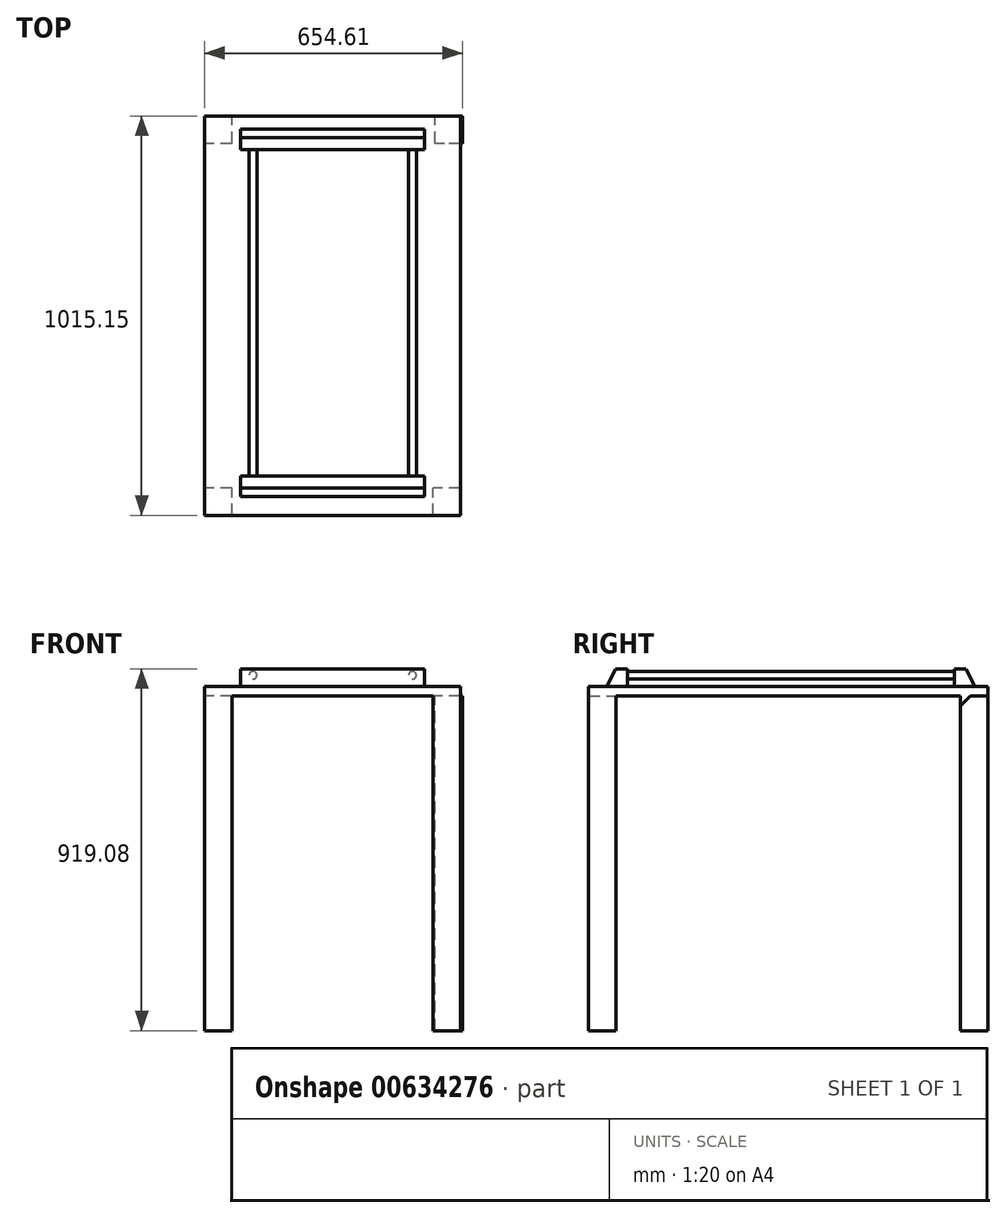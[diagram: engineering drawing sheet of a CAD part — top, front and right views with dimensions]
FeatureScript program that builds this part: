
annotation { "Feature Type Name" : "Feature", "Feature Type Description" : "" }
export const myFeature = defineFeature(function(context is Context, id is Id, definition is map)
    precondition{}
    {
        {
            var Q0;
            Q0=qCreatedBy(makeId("Front.planeOp"),FACE);
            var sketch = newSketch(context, id + "F0", { "sketchPlane" : qUnion([Q0])});
            skCircle(sketch, "E0", {"center": v(-202.55, -35.12) * mm, "radius": 9.95 * mm});
            skSolve(sketch);
        }
        {
            var Q0;
            Q0=qCreatedBy(makeId("Right.planeOp"),FACE);
            var Q1;
            Q1=sQuery(id+"F0.wireOp",VERTEX,"E0.center");
            cPlane(context, id + "F1", {"entities" : qUnion([Q0, Q1]), "cplaneType" : CPlaneType.PLANE_POINT, "offset" : 25 * mm, "width" : 150 * mm, "height" : 150 * mm});
        }
        {
            var Q0;
            Q0=qCreatedBy(makeId("Front.planeOp"),FACE);
            cPlane(context, id + "F2", {"entities" : qUnion([Q0]), "cplaneType" : CPlaneType.OFFSET, "offset" : 242.37 * mm, "width" : 150 * mm, "height" : 150 * mm});
        }
        {
            var Q0;
            Q0=qCreatedBy(id+"F1.planeOp",FACE);
            var sketch = newSketch(context, id + "F3", { "sketchPlane" : qUnion([Q0])});
            skLineSegment(sketch, "E1", {"start": v(0, -35.42) * mm, "end": v(172.63, -35.42) * mm});
            skLineSegment(sketch, "E2", {"start": v(0, -35.42) * mm, "end": v(-657.37, -35.42) * mm});
            skSolve(sketch);
        }
        {
            var Q0;
            Q0=makeQuery(id+"F0.imprint","IMPRINT",FACE,{"disambiguationData":[TD([[makeQuery(id+"F0.imprint","IMPRINT",EDGE,{"derivedFrom":sQuery(id+"F0.wireOp",EDGE,"E0")}),1.0]])]});
            var Q1;
            Q1=sQuery(id+"F3.wireOp",EDGE,"E2");
            var Q2;
            Q2=sQuery(id+"F3.wireOp",EDGE,"E1");
            sweep(context, id + "F4", {"profiles" : qUnion([Q0]), "path" : qUnion([Q1, Q2])});
        }
        {
            var Q0;
            Q0=makeQuery(id+"F4.opSweep","SWEPT_BODY",BODY,{"disambiguationData":[OSD([sQuery(id+"F0.wireOp",EDGE,"E0"),sQuery(id+"F3.wireOp",EDGE,"E1")])]});
            var Q1;
            Q1=qCreatedBy(makeId("Right.planeOp"),FACE);
            mirror(context, id + "F5", {"operationType" : NewBodyOperationType.ADD, "entities" : qUnion([Q0]), "mirrorPlane" : qUnion([Q1])});
        }
        {
            var Q0;
            Q0=makeQuery(id+"F5.opPattern","COPY",FACE,{"derivedFrom":makeQuery(id+"F4.opSweep","CAP_FACE",FACE,{"disambiguationData":[OSD([sQuery(id+"F0.wireOp",EDGE,"E0"),sQuery(id+"F3.wireOp",VERTEX,"E1.end")])],"isStart":true}),"instanceName":"1"});
            var sketch = newSketch(context, id + "F6", { "sketchPlane" : qUnion([Q0])});
            skLineSegment(sketch, "E3.bottom", {"start": v(-233.82, -19.03) * mm, "end": v(0, -19.03) * mm});
            skLineSegment(sketch, "E3.top", {"start": v(-233.82, -63.11) * mm, "end": v(0, -63.11) * mm});
            skLineSegment(sketch, "E3.left", {"start": v(-233.82, -19.03) * mm, "end": v(-233.82, -63.11) * mm});
            skLineSegment(sketch, "E4.MirrorCS", {"start": v(233.82, -19.03) * mm, "end": v(233.82, -63.11) * mm});
            skLineSegment(sketch, "E5.MirrorCS", {"start": v(233.82, -19.03) * mm, "end": v(0, -19.03) * mm});
            skLineSegment(sketch, "E6.MirrorCS", {"start": v(233.82, -63.11) * mm, "end": v(0, -63.11) * mm});
            skSolve(sketch);
        }
        {
            var Q0;
            Q0 = qSketchRegion(id + "F6", true);
            extrude(context, id + "F7", {"entities" : qUnion([Q0]), "depth" : 55 * mm, "offsetDistance" : 25 * mm});
        }
        {
            var Q0;
            Q0=makeQuery(id+"F7.opExtrude","CAP_EDGE",EDGE,{"disambiguationData":[OSD([sQuery(id+"F6.wireOp",EDGE,"E3.bottom"),sQuery(id+"F6.wireOp",EDGE,"E5.MirrorCS")])],"isStart":false});
            chamfer(context, id + "F8", {"entities" : qUnion([Q0]), "chamferType" : ChamferType.TWO_OFFSETS, "width1" : 25 * mm, "oppositeDirection" : false, "width2" : 50 * mm, "tangentPropagation" : true});
        }
        {
            var Q0;
            Q0=makeQuery(id+"F7.opExtrude","SWEPT_BODY",BODY,{"disambiguationData":[OSD([sQuery(id+"F6.wireOp",EDGE,"E3.bottom"),sQuery(id+"F6.wireOp",EDGE,"E3.top"),sQuery(id+"F6.wireOp",EDGE,"E3.left"),sQuery(id+"F6.wireOp",EDGE,"E4.MirrorCS"),sQuery(id+"F6.wireOp",EDGE,"E5.MirrorCS"),sQuery(id+"F6.wireOp",EDGE,"E6.MirrorCS")])]});
            var Q1;
            Q1=qCreatedBy(id+"F2.planeOp",FACE);
            mirror(context, id + "F9", {"entities" : qUnion([Q0]), "mirrorPlane" : qUnion([Q1])});
        }
        {
            var Q0;
            Q0=makeQuery(id+"F9.opPattern","COPY",FACE,{"derivedFrom":makeQuery(id+"F7.opExtrude","SWEPT_FACE",FACE,{"disambiguationData":[OSD([sQuery(id+"F6.wireOp",EDGE,"E3.top"),sQuery(id+"F6.wireOp",EDGE,"E6.MirrorCS")])]}),"instanceName":"1"});
            var sketch = newSketch(context, id + "F10", { "sketchPlane" : qUnion([Q0])});
            skLineSegment(sketch, "E7.bottom", {"start": v(325.02, 756.89) * mm, "end": v(-325.02, 756.89) * mm});
            skLineSegment(sketch, "E7.top", {"start": v(325.02, -258.26) * mm, "end": v(-325.02, -258.26) * mm});
            skLineSegment(sketch, "E7.left", {"start": v(325.02, 756.89) * mm, "end": v(325.02, -258.26) * mm});
            skLineSegment(sketch, "E7.right", {"start": v(-325.02, 756.89) * mm, "end": v(-325.02, -258.26) * mm});
            skPoint(sketch, "E7.middle", {"position": v(0, 249.31) * mm});
            skPoint(sketch, "E7.middle.positionSnap0", {"position": v(0, 657.37) * mm});
            skPoint(sketch, "E7.centerSnap0", {"position": v(0, 657.37) * mm});
            skSolve(sketch);
        }
        {
            var Q0;
            Q0 = qSketchRegion(id + "F10", true);
            extrude(context, id + "F11", {"entities" : qUnion([Q0]), "depth" : 25 * mm, "offsetDistance" : 25 * mm});
        }
        {
            var Q0;
            Q0=makeQuery(id+"F11.opExtrude","CAP_FACE",FACE,{"disambiguationData":[OSD([sQuery(id+"F10.wireOp",EDGE,"E7.bottom"),sQuery(id+"F10.wireOp",EDGE,"E7.top"),sQuery(id+"F10.wireOp",EDGE,"E7.left"),sQuery(id+"F10.wireOp",EDGE,"E7.right")])],"isStart":false});
            var sketch = newSketch(context, id + "F12", { "sketchPlane" : qUnion([Q0])});
            skLineSegment(sketch, "E8.bottom", {"start": v(325.02, 756.89) * mm, "end": v(255.02, 756.89) * mm});
            skLineSegment(sketch, "E8.top", {"start": v(325.02, 686.89) * mm, "end": v(255.02, 686.89) * mm});
            skLineSegment(sketch, "E8.left", {"start": v(325.02, 756.89) * mm, "end": v(325.02, 686.89) * mm});
            skLineSegment(sketch, "E8.right", {"start": v(255.02, 756.89) * mm, "end": v(255.02, 686.89) * mm});
            skLineSegment(sketch, "E9.bottom", {"start": v(329.59, -188.26) * mm, "end": v(259.59, -188.26) * mm});
            skLineSegment(sketch, "E9.top", {"start": v(329.59, -258.26) * mm, "end": v(259.59, -258.26) * mm});
            skLineSegment(sketch, "E9.left", {"start": v(329.59, -188.26) * mm, "end": v(329.59, -258.26) * mm});
            skLineSegment(sketch, "E9.right", {"start": v(259.59, -188.26) * mm, "end": v(259.59, -258.26) * mm});
            skLineSegment(sketch, "E10.bottom", {"start": v(-255.02, -188.26) * mm, "end": v(-325.02, -188.26) * mm});
            skLineSegment(sketch, "E10.top", {"start": v(-255.02, -258.26) * mm, "end": v(-325.02, -258.26) * mm});
            skLineSegment(sketch, "E10.left", {"start": v(-255.02, -188.26) * mm, "end": v(-255.02, -258.26) * mm});
            skLineSegment(sketch, "E10.right", {"start": v(-325.02, -188.26) * mm, "end": v(-325.02, -258.26) * mm});
            skLineSegment(sketch, "E11.bottom", {"start": v(-255.02, 756.89) * mm, "end": v(-325.02, 756.89) * mm});
            skLineSegment(sketch, "E11.top", {"start": v(-255.02, 686.89) * mm, "end": v(-325.02, 686.89) * mm});
            skLineSegment(sketch, "E11.left", {"start": v(-255.02, 756.89) * mm, "end": v(-255.02, 686.89) * mm});
            skLineSegment(sketch, "E11.right", {"start": v(-325.02, 756.89) * mm, "end": v(-325.02, 686.89) * mm});
            skSolve(sketch);
        }
        {
            var Q0;
            Q0 = qSketchRegion(id + "F12", true);
            extrude(context, id + "F13", {"entities" : qUnion([Q0]), "operationType" : NewBodyOperationType.ADD, "depth" : 850 * mm, "offsetDistance" : 25 * mm});
        }
        {
            var Q0;
            Q0=makeQuery(id+"F13.opExtrude","CAP_EDGE",EDGE,{"disambiguationData":[OSD([sQuery(id+"F12.wireOp",EDGE,"E10.left")])],"isStart":true});
            var Q1;
            Q1=makeQuery(id+"F13.opExtrude","CAP_EDGE",EDGE,{"disambiguationData":[OSD([sQuery(id+"F12.wireOp",EDGE,"E10.bottom")])],"isStart":true});
            var Q2;
            Q2=makeQuery(id+"F13.opExtrude","CAP_EDGE",EDGE,{"disambiguationData":[OSD([sQuery(id+"F12.wireOp",EDGE,"E11.left")])],"isStart":true});
            var Q3;
            {var subQ0=sQuery(id+"F12.wireOp",EDGE,"E9.bottom");Q3=makeQuery(id+"F13.boolean.opBoolean","SPLIT",EDGE,{"disambiguationData":[topologyDisambiguationEdgeConnected([makeQuery(id+"F11.opExtrude","CAP_FACE",FACE,{"disambiguationData":[OSD([sQuery(id+"F10.wireOp",EDGE,"E7.bottom"),sQuery(id+"F10.wireOp",EDGE,"E7.top"),sQuery(id+"F10.wireOp",EDGE,"E7.left"),sQuery(id+"F10.wireOp",EDGE,"E7.right")])],"isStart":false})])],"derivedFrom":makeQuery(id+"F13.opExtrude","CAP_EDGE",EDGE,{"disambiguationData":[OSD([subQ0])],"isStart":true})});}
            var Q4;
            Q4=makeQuery(id+"F13.opExtrude","CAP_EDGE",EDGE,{"disambiguationData":[OSD([sQuery(id+"F12.wireOp",EDGE,"E9.right")])],"isStart":true});
            var Q5;
            Q5=makeQuery(id+"F13.opExtrude","CAP_EDGE",EDGE,{"disambiguationData":[OSD([sQuery(id+"F12.wireOp",EDGE,"E8.right")])],"isStart":true});
            var Q6;
            Q6=makeQuery(id+"F13.opExtrude","CAP_EDGE",EDGE,{"disambiguationData":[OSD([sQuery(id+"F12.wireOp",EDGE,"E8.top")])],"isStart":true});
            var Q7;
            Q7=makeQuery(id+"F13.opExtrude","CAP_EDGE",EDGE,{"disambiguationData":[OSD([sQuery(id+"F12.wireOp",EDGE,"E11.top")])],"isStart":true});
            chamfer(context, id + "F14", {"entities" : qUnion([Q0, Q1, Q2, Q3, Q4, Q5, Q6, Q7]), "width" : 25 * mm, "tangentPropagation" : true});
        }
    });
